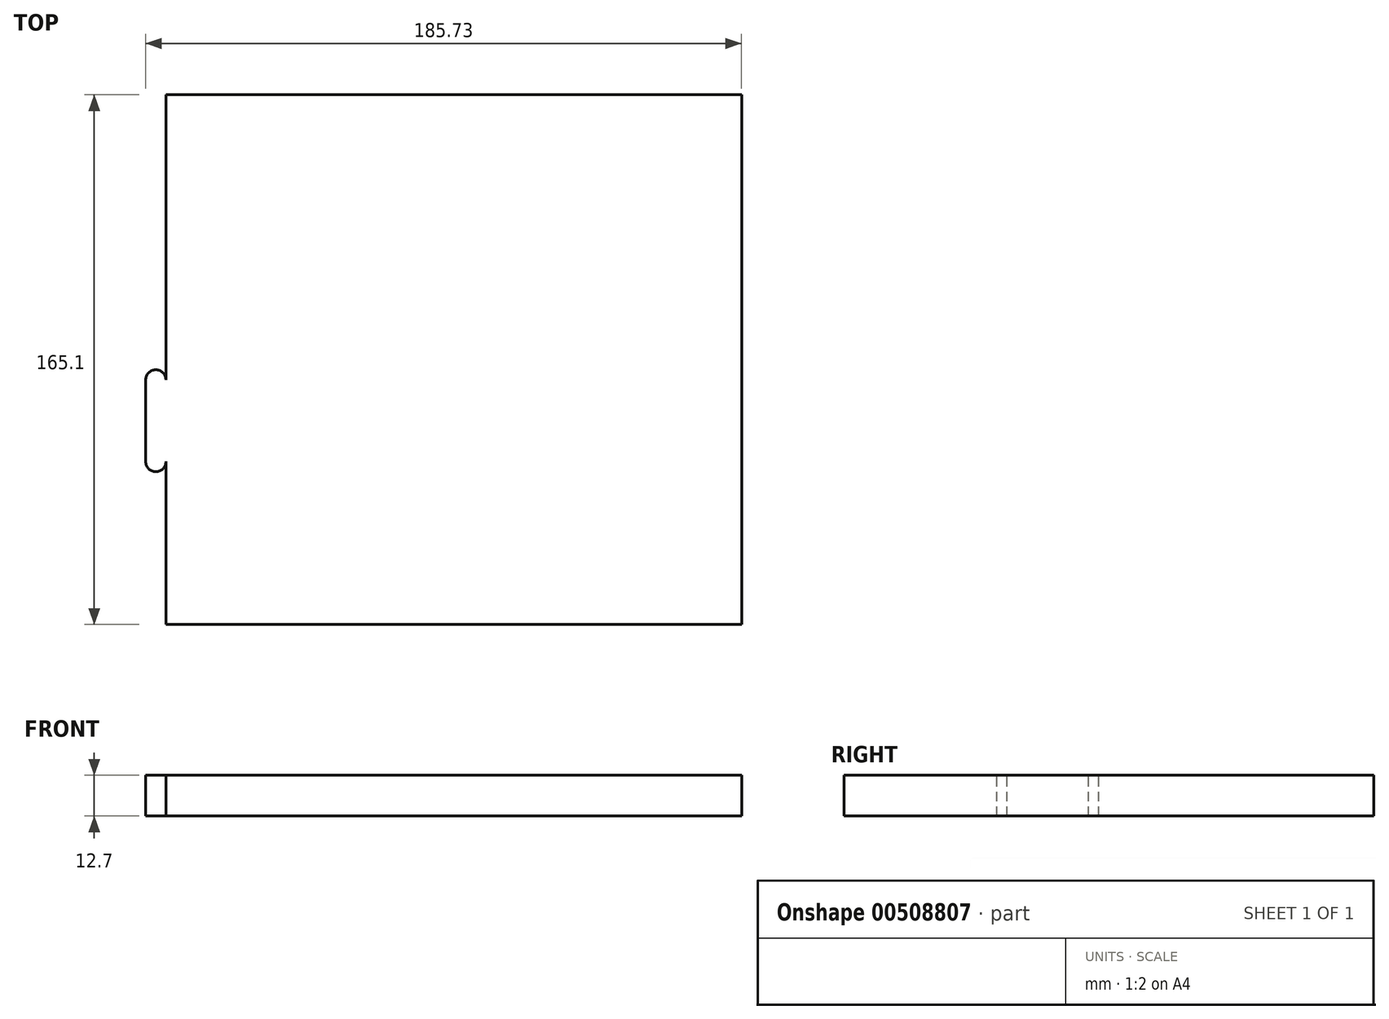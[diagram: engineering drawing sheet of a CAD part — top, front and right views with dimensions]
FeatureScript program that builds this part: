
annotation { "Feature Type Name" : "Feature", "Feature Type Description" : "" }
export const myFeature = defineFeature(function(context is Context, id is Id, definition is map)
    precondition{}
    {
        {
            var Q0;
            Q0=qCreatedBy(makeId("Top.planeOp"),FACE);
            var sketch = newSketch(context, id + "F0", { "sketchPlane" : qUnion([Q0])});
            skLineSegment(sketch, "E0.bottom", {"start": v(0, 0) * mm, "end": v(-228.6, 0) * mm});
            skLineSegment(sketch, "E0.top", {"start": v(0, 177.8) * mm, "end": v(-228.6, 177.8) * mm});
            skLineSegment(sketch, "E0.left", {"start": v(0, 0) * mm, "end": v(0, 177.8) * mm});
            skLineSegment(sketch, "E0.right", {"start": v(-228.6, 0) * mm, "end": v(-228.6, 177.8) * mm});
            skLineSegment(sketch, "E1", {"start": v(-228.6, 88.9) * mm, "end": v(0, 88.9) * mm, "construction": true});
            skSolve(sketch);
        }
        {
            var Q0;
            Q0=makeQuery(id+"F0.imprint","IMPRINT",FACE,{"disambiguationData":[TD([[makeQuery(id+"F0.imprint","IMPRINT",EDGE,{"derivedFrom":sQuery(id+"F0.wireOp",EDGE,"E0.bottom")}),-1.0]])]});
            extrude(context, id + "F1", {"entities" : qUnion([Q0]), "depth" : 12.7 * mm, "offsetDistance" : 25.4 * mm});
        }
        {
            var Q0;
            Q0=makeQuery(id+"F1.opExtrude","CAP_FACE",FACE,{"disambiguationData":[OSD([sQuery(id+"F0.wireOp",EDGE,"E0.bottom"),sQuery(id+"F0.wireOp",EDGE,"E0.top"),sQuery(id+"F0.wireOp",EDGE,"E0.left"),sQuery(id+"F0.wireOp",EDGE,"E0.right")])],"isStart":false});
            var sketch = newSketch(context, id + "F2", { "sketchPlane" : qUnion([Q0])});
            skPoint(sketch, "E2", {"position": v(-12.7, 165.1) * mm});
            skPoint(sketch, "E3", {"position": v(-12.7, 38.1) * mm});
            skLineSegment(sketch, "E4", {"start": v(-114.3, 0) * mm, "end": v(-114.3, 177.8) * mm, "construction": true});
            skPoint(sketch, "E5.MirrorP", {"position": v(-215.9, 38.1) * mm});
            skPoint(sketch, "E6.MirrorP", {"position": v(-215.9, 165.1) * mm});
            skSolve(sketch);
        }
        {
            var Q0;
            Q0=sQuery(id+"F2.wireOp",VERTEX,"E3");
            var Q1;
            Q1=sQuery(id+"F2.wireOp",VERTEX,"E2");
            var Q2;
            Q2=sQuery(id+"F2.wireOp",VERTEX,"E5.MirrorP");
            var Q3;
            Q3=sQuery(id+"F2.wireOp",VERTEX,"E6.MirrorP");
            var Q4;
            Q4=makeQuery(id+"F1.opExtrude","SWEPT_BODY",BODY,{"disambiguationData":[OSD([sQuery(id+"F0.wireOp",EDGE,"E0.bottom"),sQuery(id+"F0.wireOp",EDGE,"E0.top"),sQuery(id+"F0.wireOp",EDGE,"E0.left"),sQuery(id+"F0.wireOp",EDGE,"E0.right")])]});
            hole(context, id + "F3", {"style" : HoleStyle.SIMPLE, "endStyle" : HoleEndStyle.THROUGH, "standardTappedOrClearance" : lookupTablePath({ "standard" : "ANSI", "fit" : "Normal (ASME)", "size" : "#10", "type" : "Clearance" }), "standardBlindInLast" : lookupTablePath({ "fit" : "Free", "standard" : "ANSI", "size" : "#10", "type" : "Clearance" }), "holeDiameter" : 5.1 * mm, "isTappedThrough" : true, "tappedDepth" : 12.7 * mm, "tapClearance" : 3, "locations" : qUnion([Q0, Q1, Q2, Q3]), "scope" : qUnion([Q4])});
        }
        {
            var Q0;
            Q0=makeQuery(id+"F1.opExtrude","CAP_FACE",FACE,{"disambiguationData":[OSD([sQuery(id+"F0.wireOp",EDGE,"E0.bottom"),sQuery(id+"F0.wireOp",EDGE,"E0.top"),sQuery(id+"F0.wireOp",EDGE,"E0.left"),sQuery(id+"F0.wireOp",EDGE,"E0.right")])],"isStart":false});
            var sketch = newSketch(context, id + "F4", { "sketchPlane" : qUnion([Q0])});
            skLineSegment(sketch, "E7.bottom", {"start": v(-18.26, 120.65) * mm, "end": v(-24.6, 120.65) * mm, "construction": true});
            skLineSegment(sketch, "E7.top", {"start": v(-18.26, 146.05) * mm, "end": v(-24.6, 146.05) * mm, "construction": true});
            skLineSegment(sketch, "E7.left", {"start": v(-18.26, 120.65) * mm, "end": v(-18.26, 146.05) * mm});
            skLineSegment(sketch, "E7.right", {"start": v(-24.6, 120.65) * mm, "end": v(-24.6, 146.05) * mm});
            skLineSegment(sketch, "E8.bottom", {"start": v(-18.26, 82.55) * mm, "end": v(-24.6, 82.55) * mm, "construction": true});
            skLineSegment(sketch, "E8.left", {"start": v(-18.26, 82.55) * mm, "end": v(-18.26, 57.15) * mm});
            skLineSegment(sketch, "E8.right", {"start": v(-24.6, 82.55) * mm, "end": v(-24.6, 57.15) * mm});
            skArc(sketch, "E9", {"start": v(-18.26, 120.65) * mm, "mid": v(-21.43, 117.47) * mm, "end": v(-24.6, 120.65) * mm});
            skArc(sketch, "E10", {"start": v(-18.26, 146.05) * mm, "mid": v(-21.43, 149.22) * mm, "end": v(-24.6, 146.05) * mm});
            skArc(sketch, "E11", {"start": v(-18.26, 82.55) * mm, "mid": v(-21.43, 85.72) * mm, "end": v(-24.6, 82.55) * mm});
            skArc(sketch, "E12", {"start": v(-18.26, 57.15) * mm, "mid": v(-21.43, 53.98) * mm, "end": v(-24.6, 57.15) * mm});
            skLineSegment(sketch, "E13", {"start": v(-24.6, 57.15) * mm, "end": v(-18.26, 57.15) * mm, "construction": true});
            skLineSegment(sketch, "E14", {"start": v(-114.3, 177.8) * mm, "end": v(-114.3, 0) * mm, "construction": true});
            skLineSegment(sketch, "E15.MirrorCS", {"start": v(-210.34, 146.05) * mm, "end": v(-204, 146.05) * mm, "construction": true});
            skLineSegment(sketch, "E16.MirrorCS", {"start": v(-210.34, 120.65) * mm, "end": v(-204, 120.65) * mm, "construction": true});
            skArc(sketch, "E17.MirrorCS", {"start": v(-210.34, 120.65) * mm, "mid": v(-207.17, 117.47) * mm, "end": v(-204, 120.65) * mm});
            skLineSegment(sketch, "E18.MirrorCS", {"start": v(-210.34, 57.15) * mm, "end": v(-204, 57.15) * mm, "construction": true});
            skArc(sketch, "E19.MirrorCS", {"start": v(-210.34, 82.55) * mm, "mid": v(-207.17, 85.72) * mm, "end": v(-204, 82.55) * mm});
            skLineSegment(sketch, "E20.MirrorCS", {"start": v(-204, 82.55) * mm, "end": v(-210.34, 82.55) * mm, "construction": true});
            skLineSegment(sketch, "E21.MirrorCS", {"start": v(-204, 120.65) * mm, "end": v(-204, 146.05) * mm});
            skLineSegment(sketch, "E22.MirrorCS", {"start": v(-204, 82.55) * mm, "end": v(-204, 57.15) * mm});
            skArc(sketch, "E23.MirrorCS", {"start": v(-210.34, 57.15) * mm, "mid": v(-207.17, 53.98) * mm, "end": v(-204, 57.15) * mm});
            skLineSegment(sketch, "E24.MirrorCS", {"start": v(-210.34, 82.55) * mm, "end": v(-210.34, 57.15) * mm});
            skLineSegment(sketch, "E25.MirrorCS", {"start": v(-210.34, 120.65) * mm, "end": v(-210.34, 146.05) * mm});
            skArc(sketch, "E26.MirrorCS", {"start": v(-210.34, 146.05) * mm, "mid": v(-207.17, 149.22) * mm, "end": v(-204, 146.05) * mm});
            skLineSegment(sketch, "E27.bottom", {"start": v(-204, 171.45) * mm, "end": v(-24.6, 171.45) * mm});
            skLineSegment(sketch, "E27.top", {"start": v(-204, 6.35) * mm, "end": v(-24.6, 6.35) * mm});
            skLineSegment(sketch, "E27.left", {"start": v(-204, 171.45) * mm, "end": v(-204, 6.35) * mm});
            skLineSegment(sketch, "E27.right", {"start": v(-24.6, 171.45) * mm, "end": v(-24.6, 6.35) * mm});
            skPoint(sketch, "E28", {"position": v(-114.3, 171.45) * mm});
            skPoint(sketch, "E29", {"position": v(-204, 88.9) * mm});
            skLineSegment(sketch, "E30", {"start": v(-228.6, 88.9) * mm, "end": v(0, 88.9) * mm, "construction": true});
            skSolve(sketch);
        }
        {
            var Q0;
            Q0=makeQuery(id+"F4.imprint","IMPRINT",FACE,{"disambiguationData":[TD([[makeQuery(id+"F4.imprint","IMPRINT",EDGE,{"derivedFrom":sQuery(id+"F4.wireOp",EDGE,"E7.left")}),1.0]])]});
            var Q1;
            Q1=makeQuery(id+"F4.imprint","IMPRINT",FACE,{"disambiguationData":[TD([[makeQuery(id+"F4.imprint","IMPRINT",EDGE,{"derivedFrom":sQuery(id+"F4.wireOp",EDGE,"E8.left")}),-1.0]])]});
            var Q2;
            {var subQ0=sQuery(id+"F4.wireOp",EDGE,"E17.MirrorCS");Q2=makeQuery(id+"F4.imprint","IMPRINT",FACE,{"disambiguationData":[TD([[makeQuery(id+"F4.imprint","IMPRINT",EDGE,{"derivedFrom":subQ0}),1.0]])]});}
            var Q3;
            {var subQ0=sQuery(id+"F4.wireOp",EDGE,"E19.MirrorCS");Q3=makeQuery(id+"F4.imprint","IMPRINT",FACE,{"disambiguationData":[TD([[makeQuery(id+"F4.imprint","IMPRINT",EDGE,{"derivedFrom":subQ0}),-1.0]])]});}
            extrude(context, id + "F5", {"entities" : qUnion([Q0, Q1, Q2, Q3]), "operationType" : NewBodyOperationType.REMOVE, "endBound" : BoundingType.THROUGH_ALL, "oppositeDirection" : true, "depth" : 25.4 * mm, "offsetDistance" : 25.4 * mm});
        }
    });
